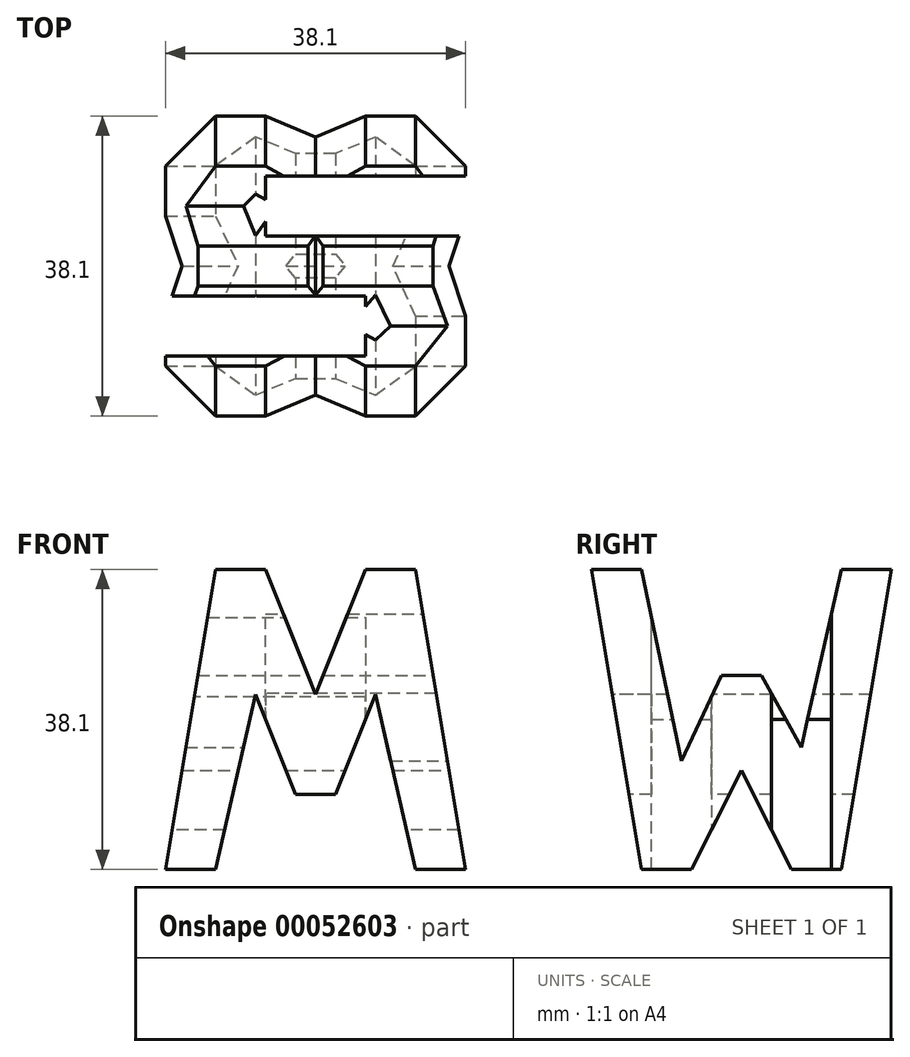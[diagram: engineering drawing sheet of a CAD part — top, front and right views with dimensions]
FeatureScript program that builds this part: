
annotation { "Feature Type Name" : "Feature", "Feature Type Description" : "" }
export const myFeature = defineFeature(function(context is Context, id is Id, definition is map)
    precondition{}
    {
        {
            var Q0;
            Q0=qCreatedBy(makeId("Front.planeOp"),FACE);
            var sketch = newSketch(context, id + "F0", { "sketchPlane" : qUnion([Q0])});
            skLineSegment(sketch, "E0.bottom", {"start": v(0, 0) * mm, "end": v(38.1, 0) * mm});
            skLineSegment(sketch, "E0.top", {"start": v(0, 38.1) * mm, "end": v(38.1, 38.1) * mm});
            skLineSegment(sketch, "E0.left", {"start": v(0, 0) * mm, "end": v(0, 38.1) * mm});
            skLineSegment(sketch, "E0.right", {"start": v(38.1, 0) * mm, "end": v(38.1, 38.1) * mm});
            skSolve(sketch);
        }
        {
            var Q0;
            Q0 = qSketchRegion(id + "F0", true);
            extrude(context, id + "F1", {"entities" : qUnion([Q0]), "depth" : 38.1 * mm});
        }
        {
            var Q0;
            Q0=qCreatedBy(makeId("Front.planeOp"),FACE);
            cPlane(context, id + "F2", {"entities" : qUnion([Q0]), "cplaneType" : CPlaneType.OFFSET, "offset" : 38.1 * mm, "width" : 152.4 * mm, "height" : 152.4 * mm});
        }
        {
            var Q0;
            Q0=qCreatedBy(makeId("Right.planeOp"),FACE);
            cPlane(context, id + "F3", {"entities" : qUnion([Q0]), "cplaneType" : CPlaneType.OFFSET, "offset" : 38.1 * mm, "width" : 152.4 * mm, "height" : 152.4 * mm});
        }
        {
            var Q0;
            Q0=qCreatedBy(makeId("Top.planeOp"),FACE);
            cPlane(context, id + "F4", {"entities" : qUnion([Q0]), "cplaneType" : CPlaneType.OFFSET, "offset" : 38.1 * mm, "width" : 152.4 * mm, "height" : 152.4 * mm});
        }
        {
            var Q0;
            Q0=qCreatedBy(id+"F3.planeOp",FACE);
            var sketch = newSketch(context, id + "F5", { "sketchPlane" : qUnion([Q0])});
            skLineSegment(sketch, "E1.bottom", {"start": v(0, 0) * mm, "end": v(-38.1, 0) * mm});
            skLineSegment(sketch, "E1.top", {"start": v(0, 38.1) * mm, "end": v(-38.1, 38.1) * mm});
            skLineSegment(sketch, "E1.left", {"start": v(0, 0) * mm, "end": v(0, 38.1) * mm});
            skLineSegment(sketch, "E1.right", {"start": v(-38.1, 0) * mm, "end": v(-38.1, 38.1) * mm});
            skLineSegment(sketch, "E2", {"start": v(-38.1, 38.1) * mm, "end": v(-31.75, 0) * mm});
            skLineSegment(sketch, "E3", {"start": v(-25.4, 0) * mm, "end": v(-19.05, 12.56) * mm});
            skLineSegment(sketch, "E4", {"start": v(-19.05, 12.56) * mm, "end": v(-12.7, 0) * mm});
            skLineSegment(sketch, "E5", {"start": v(-6.35, 0) * mm, "end": v(0, 38.1) * mm});
            skLineSegment(sketch, "E6", {"start": v(-31.75, 38.1) * mm, "end": v(-26.67, 13.79) * mm});
            skLineSegment(sketch, "E7", {"start": v(-26.67, 13.79) * mm, "end": v(-21.6, 24.62) * mm});
            skLineSegment(sketch, "E8", {"start": v(-21.6, 24.62) * mm, "end": v(-16.51, 24.62) * mm});
            skLineSegment(sketch, "E9", {"start": v(-16.51, 24.62) * mm, "end": v(-11.43, 15.5) * mm});
            skLineSegment(sketch, "E10", {"start": v(-11.43, 15.5) * mm, "end": v(-6.35, 38.1) * mm});
            skSolve(sketch);
        }
        {
            var Q0;
            {var subQ0=sQuery(id+"F5.wireOp",EDGE,"E6");Q0=makeQuery(id+"F5.imprint","IMPRINT",FACE,{"disambiguationData":[TD([[makeQuery(id+"F5.imprint","IMPRINT",EDGE,{"derivedFrom":subQ0}),1.0]])]});}
            var Q1;
            {var subQ0=sQuery(id+"F5.wireOp",EDGE,"E1.right");Q1=makeQuery(id+"F5.imprint","IMPRINT",FACE,{"disambiguationData":[TD([[makeQuery(id+"F5.imprint","IMPRINT",EDGE,{"derivedFrom":subQ0}),-1.0]])]});}
            var Q2;
            {var subQ0=sQuery(id+"F5.wireOp",EDGE,"E3");Q2=makeQuery(id+"F5.imprint","IMPRINT",FACE,{"disambiguationData":[TD([[makeQuery(id+"F5.imprint","IMPRINT",EDGE,{"derivedFrom":subQ0}),-1.0]])]});}
            var Q3;
            {var subQ0=sQuery(id+"F5.wireOp",EDGE,"E1.left");Q3=makeQuery(id+"F5.imprint","IMPRINT",FACE,{"disambiguationData":[TD([[makeQuery(id+"F5.imprint","IMPRINT",EDGE,{"derivedFrom":subQ0}),1.0]])]});}
            extrude(context, id + "F6", {"entities" : qUnion([Q0, Q1, Q2, Q3]), "operationType" : NewBodyOperationType.REMOVE, "oppositeDirection" : true, "depth" : 38.1 * mm});
        }
        {
            var Q0;
            Q0=qCreatedBy(id+"F2.planeOp",FACE);
            var sketch = newSketch(context, id + "F7", { "sketchPlane" : qUnion([Q0])});
            skLineSegment(sketch, "E11.bottom", {"start": v(0, 0) * mm, "end": v(38.1, 0) * mm});
            skLineSegment(sketch, "E11.top", {"start": v(0, 38.1) * mm, "end": v(38.1, 38.1) * mm});
            skLineSegment(sketch, "E11.left", {"start": v(0, 0) * mm, "end": v(0, 38.1) * mm});
            skLineSegment(sketch, "E11.right", {"start": v(38.1, 0) * mm, "end": v(38.1, 38.1) * mm});
            skLineSegment(sketch, "E12", {"start": v(0, 0) * mm, "end": v(6.35, 38.1) * mm});
            skLineSegment(sketch, "E13", {"start": v(12.7, 38.1) * mm, "end": v(19.05, 22.22) * mm});
            skLineSegment(sketch, "E14", {"start": v(19.05, 22.22) * mm, "end": v(25.4, 38.1) * mm});
            skLineSegment(sketch, "E15", {"start": v(31.75, 38.1) * mm, "end": v(38.1, 0) * mm});
            skLineSegment(sketch, "E16", {"start": v(6.35, 0) * mm, "end": v(11.43, 22.23) * mm});
            skLineSegment(sketch, "E17", {"start": v(11.43, 22.23) * mm, "end": v(16.51, 9.52) * mm});
            skLineSegment(sketch, "E18", {"start": v(16.51, 9.52) * mm, "end": v(21.59, 9.52) * mm});
            skLineSegment(sketch, "E19", {"start": v(21.59, 9.52) * mm, "end": v(26.67, 22.22) * mm});
            skLineSegment(sketch, "E20", {"start": v(26.67, 22.23) * mm, "end": v(31.75, 0) * mm});
            skSolve(sketch);
        }
        {
            var Q0;
            {var subQ0=sQuery(id+"F7.wireOp",EDGE,"E11.left");Q0=makeQuery(id+"F7.imprint","IMPRINT",FACE,{"disambiguationData":[TD([[makeQuery(id+"F7.imprint","IMPRINT",EDGE,{"derivedFrom":subQ0}),-1.0]])]});}
            var Q1;
            {var subQ0=sQuery(id+"F7.wireOp",EDGE,"E16");Q1=makeQuery(id+"F7.imprint","IMPRINT",FACE,{"disambiguationData":[TD([[makeQuery(id+"F7.imprint","IMPRINT",EDGE,{"derivedFrom":subQ0}),-1.0]])]});}
            var Q2;
            {var subQ0=sQuery(id+"F7.wireOp",EDGE,"E13");Q2=makeQuery(id+"F7.imprint","IMPRINT",FACE,{"disambiguationData":[TD([[makeQuery(id+"F7.imprint","IMPRINT",EDGE,{"derivedFrom":subQ0}),1.0]])]});}
            var Q3;
            {var subQ0=sQuery(id+"F7.wireOp",EDGE,"E11.right");Q3=makeQuery(id+"F7.imprint","IMPRINT",FACE,{"disambiguationData":[TD([[makeQuery(id+"F7.imprint","IMPRINT",EDGE,{"derivedFrom":subQ0}),1.0]])]});}
            extrude(context, id + "F8", {"entities" : qUnion([Q0, Q1, Q2, Q3]), "operationType" : NewBodyOperationType.REMOVE, "oppositeDirection" : true, "depth" : 38.1 * mm});
        }
        {
            var Q0;
            Q0=qCreatedBy(id+"F4.planeOp",FACE);
            var sketch = newSketch(context, id + "F9", { "sketchPlane" : qUnion([Q0])});
            skLineSegment(sketch, "E21.bottom", {"start": v(0, 0) * mm, "end": v(38.1, 0) * mm});
            skLineSegment(sketch, "E21.top", {"start": v(0, -38.1) * mm, "end": v(38.1, -38.1) * mm});
            skLineSegment(sketch, "E21.left", {"start": v(0, 0) * mm, "end": v(0, -38.1) * mm});
            skLineSegment(sketch, "E21.right", {"start": v(38.1, 0) * mm, "end": v(38.1, -38.1) * mm});
            skLineSegment(sketch, "E22", {"start": v(38.1, -7.62) * mm, "end": v(12.7, -7.62) * mm});
            skLineSegment(sketch, "E23", {"start": v(12.7, -7.62) * mm, "end": v(12.7, -15.24) * mm});
            skLineSegment(sketch, "E24", {"start": v(12.7, -15.24) * mm, "end": v(38.1, -15.24) * mm});
            skLineSegment(sketch, "E25", {"start": v(0, -22.86) * mm, "end": v(25.4, -22.86) * mm});
            skLineSegment(sketch, "E26", {"start": v(25.4, -22.86) * mm, "end": v(25.4, -30.48) * mm});
            skLineSegment(sketch, "E27", {"start": v(25.4, -30.48) * mm, "end": v(0, -30.48) * mm});
            skSolve(sketch);
        }
        {
            var Q0;
            {var subQ0=sQuery(id+"F9.wireOp",EDGE,"E22");Q0=makeQuery(id+"F9.imprint","IMPRINT",FACE,{"disambiguationData":[TD([[makeQuery(id+"F9.imprint","IMPRINT",EDGE,{"derivedFrom":subQ0}),1.0]])]});}
            var Q1;
            {var subQ0=sQuery(id+"F9.wireOp",EDGE,"E25");Q1=makeQuery(id+"F9.imprint","IMPRINT",FACE,{"disambiguationData":[TD([[makeQuery(id+"F9.imprint","IMPRINT",EDGE,{"derivedFrom":subQ0}),-1.0]])]});}
            extrude(context, id + "F10", {"entities" : qUnion([Q0, Q1]), "operationType" : NewBodyOperationType.REMOVE, "oppositeDirection" : true, "depth" : 38.1 * mm});
        }
    });
